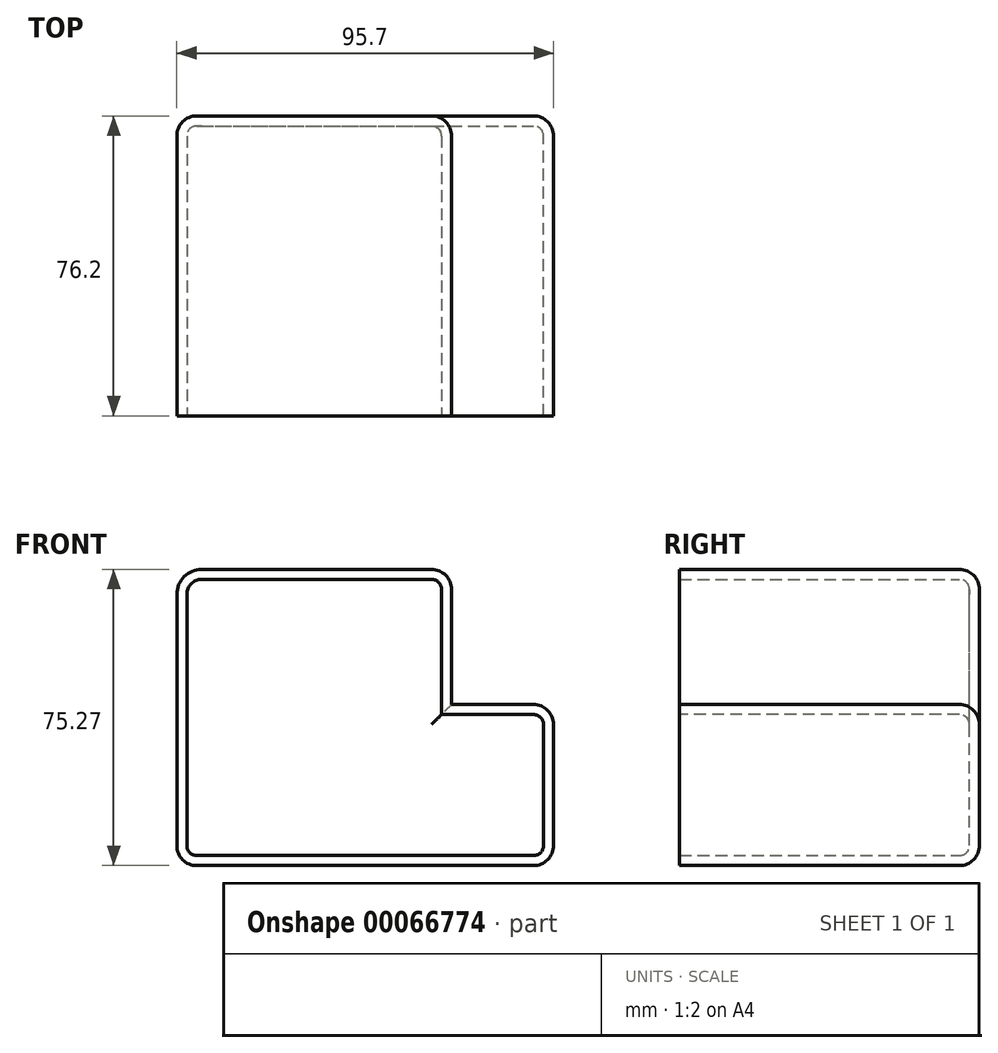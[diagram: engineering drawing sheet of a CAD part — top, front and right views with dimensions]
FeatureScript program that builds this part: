
annotation { "Feature Type Name" : "Feature", "Feature Type Description" : "" }
export const myFeature = defineFeature(function(context is Context, id is Id, definition is map)
    precondition{}
    {
        {
            var Q0;
            Q0=qCreatedBy(makeId("Front.planeOp"),FACE);
            var sketch = newSketch(context, id + "F0", { "sketchPlane" : qUnion([Q0])});
            skLineSegment(sketch, "E0.bottom", {"start": v(-74.99, 40.6) * mm, "end": v(-11.54, 40.6) * mm});
            skLineSegment(sketch, "E0.top", {"start": v(-81.34, -34.66) * mm, "end": v(14.36, -34.66) * mm});
            skLineSegment(sketch, "E0.left", {"start": v(-81.34, 34.26) * mm, "end": v(-81.34, -34.66) * mm});
            skLineSegment(sketch, "E0.right", {"start": v(14.36, 6.27) * mm, "end": v(14.36, -34.66) * mm});
            skPoint(sketch, "E1.visualSharp", {"position": v(-81.34, 40.6) * mm});
            skArc(sketch, "E1.filletArc", {"start": v(-74.99, 40.6) * mm, "mid": v(-79.48, 38.75) * mm, "end": v(-81.34, 34.26) * mm});
            skLineSegment(sketch, "E2", {"start": v(-11.54, 40.6) * mm, "end": v(-11.54, 6.27) * mm});
            skLineSegment(sketch, "E3", {"start": v(-11.54, 6.27) * mm, "end": v(14.36, 6.27) * mm});
            skSolve(sketch);
        }
        {
            var Q0;
            Q0 = qSketchRegion(id + "F0", true);
            extrude(context, id + "F1", {"entities" : qUnion([Q0]), "oppositeDirection" : true, "depth" : 76.2 * mm});
        }
        {
            var Q0;
            Q0=makeQuery(id+"F1.opExtrude","CAP_EDGE",EDGE,{"disambiguationData":[OSD([sQuery(id+"F0.wireOp",EDGE,"E0.bottom")])],"isStart":false});
            var Q1;
            Q1=makeQuery(id+"F1.opExtrude","CAP_EDGE",EDGE,{"disambiguationData":[OSD([sQuery(id+"F0.wireOp",EDGE,"E2")])],"isStart":false});
            var Q2;
            Q2=makeQuery(id+"F1.opExtrude","CAP_EDGE",EDGE,{"disambiguationData":[OSD([sQuery(id+"F0.wireOp",EDGE,"E3")])],"isStart":false});
            var Q3;
            Q3=makeQuery(id+"F1.opExtrude","CAP_EDGE",EDGE,{"disambiguationData":[OSD([sQuery(id+"F0.wireOp",EDGE,"E0.right")])],"isStart":false});
            var Q4;
            Q4=makeQuery(id+"F1.opExtrude","CAP_EDGE",EDGE,{"disambiguationData":[OSD([sQuery(id+"F0.wireOp",EDGE,"E0.left")])],"isStart":false});
            var Q5;
            Q5=makeQuery(id+"F1.opExtrude","CAP_EDGE",EDGE,{"disambiguationData":[OSD([sQuery(id+"F0.wireOp",EDGE,"E0.top")])],"isStart":false});
            var Q6;
            Q6=makeQuery(id+"F1.opExtrude","SWEPT_EDGE",EDGE,{"disambiguationData":[OSD([sQuery(id+"F0.wireOp",EDGE,"E0.left"),sQuery(id+"F0.wireOp",EDGE,"E1.filletArc")])]});
            var Q7;
            Q7=makeQuery(id+"F1.opExtrude","SWEPT_EDGE",EDGE,{"disambiguationData":[OSD([sQuery(id+"F0.wireOp",EDGE,"E0.bottom"),sQuery(id+"F0.wireOp",EDGE,"E1.filletArc")])]});
            var Q8;
            Q8=makeQuery(id+"F1.opExtrude","SWEPT_EDGE",EDGE,{"disambiguationData":[OSD([sQuery(id+"F0.wireOp",EDGE,"E0.top"),sQuery(id+"F0.wireOp",EDGE,"E0.left")])]});
            var Q9;
            Q9=makeQuery(id+"F1.opExtrude","SWEPT_EDGE",EDGE,{"disambiguationData":[OSD([sQuery(id+"F0.wireOp",EDGE,"E0.top"),sQuery(id+"F0.wireOp",EDGE,"E0.right")])]});
            var Q10;
            Q10=makeQuery(id+"F1.opExtrude","SWEPT_EDGE",EDGE,{"disambiguationData":[OSD([sQuery(id+"F0.wireOp",EDGE,"E0.right"),sQuery(id+"F0.wireOp",EDGE,"E3")])]});
            var Q11;
            Q11=makeQuery(id+"F1.opExtrude","SWEPT_EDGE",EDGE,{"disambiguationData":[OSD([sQuery(id+"F0.wireOp",EDGE,"E0.bottom"),sQuery(id+"F0.wireOp",EDGE,"E2")])]});
            var Q12;
            Q12=makeQuery(id+"F1.opExtrude","CAP_EDGE",EDGE,{"disambiguationData":[OSD([sQuery(id+"F0.wireOp",EDGE,"E1.filletArc")])],"isStart":false});
            fillet(context, id + "F2", {"entities" : qUnion([Q0, Q1, Q2, Q3, Q4, Q5, Q6, Q7, Q8, Q9, Q10, Q11, Q12]), "radius" : 5.08 * mm, "tangentPropagation" : true, "allowEdgeOverflow" : false});
        }
        {
            var Q0;
            Q0=makeQuery(id+"F1.opExtrude","CAP_FACE",FACE,{"disambiguationData":[OSD([sQuery(id+"F0.wireOp",EDGE,"E0.bottom"),sQuery(id+"F0.wireOp",EDGE,"E0.top"),sQuery(id+"F0.wireOp",EDGE,"E0.left"),sQuery(id+"F0.wireOp",EDGE,"E0.right"),sQuery(id+"F0.wireOp",EDGE,"E1.filletArc"),sQuery(id+"F0.wireOp",EDGE,"E2"),sQuery(id+"F0.wireOp",EDGE,"E3")])],"isStart":true});
            shell(context, id + "F3", {"entities" : qUnion([Q0]), "thickness" : 2.54 * mm});
        }
    });
